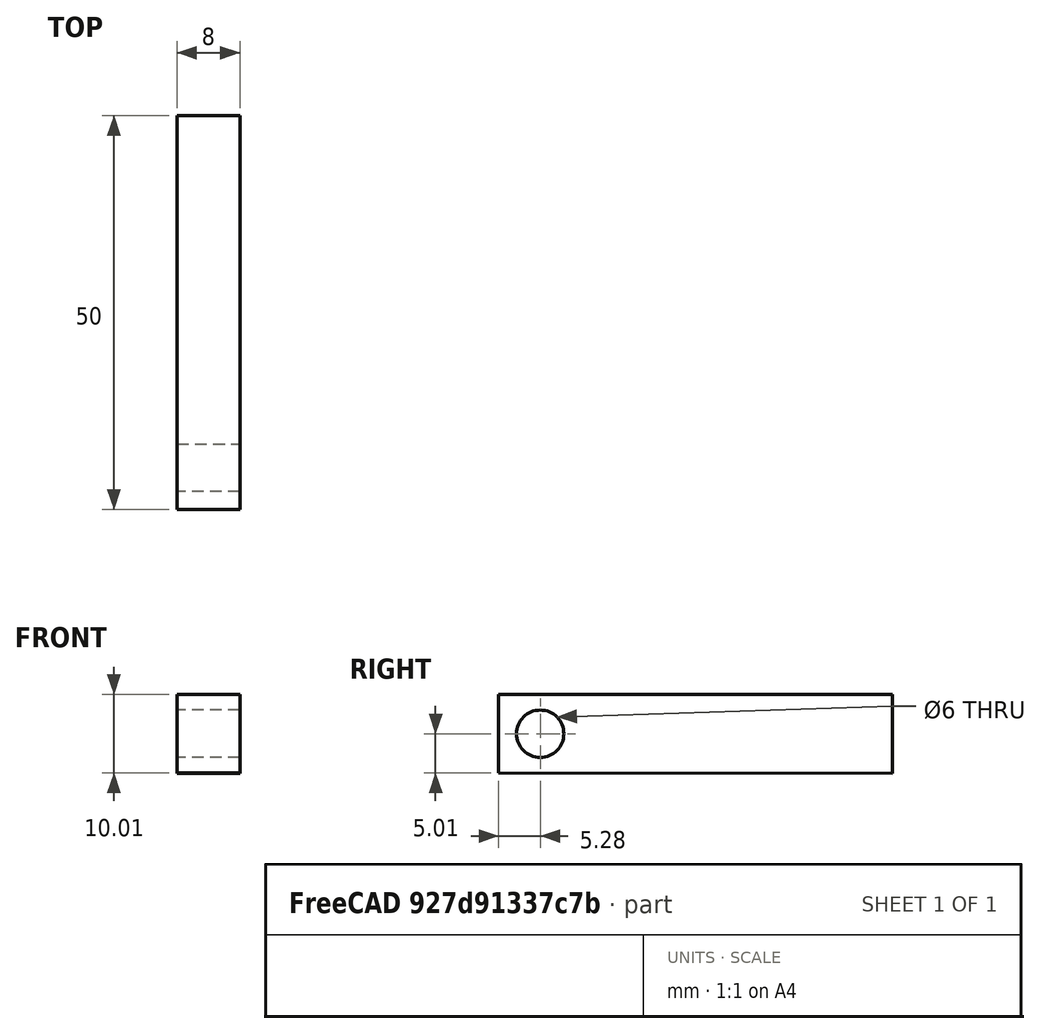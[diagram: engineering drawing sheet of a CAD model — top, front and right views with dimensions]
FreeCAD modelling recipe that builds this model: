
FCSTD DOCUMENT  (FreeCAD 0.21R33668 +26 (Git))
Label: Assembly_001
License: All rights reserved
LicenseURL: http://en.wikipedia.org/wiki/All_rights_reserved
objects: PartDesign::CoordinateSystem×6, App::DocumentObjectGroup×3, App::Part×3, Sketcher::SketchObject×2, App::Link×2, App::FeaturePython×1, PartDesign::Pad×1, PartDesign::Body×1
note: 11 computed .brp shape members not serialized (recipe doc carries the construction recipe); baked Part::Feature solids carry a one-line shape summary decoded from their .brp

FEATURE [PartDesign::CoordinateSystem] LCS_Origin
  AttacherType = Attacher::AttachEngine3D
  MapMode = 2
  Support = -> [X_Axis]
FEATURE [App::DocumentObjectGroup] Constraints
FEATURE [App::FeaturePython] Variables  # WARN: FeaturePython — macro-defined, semantics opaque (R4)
  Type = App::PropertyContainer
  rotation_bielle = 324
FEATURE [App::DocumentObjectGroup] Configurations
FEATURE [PartDesign::CoordinateSystem] LCS_0
  AttacherType = Attacher::AttachEngine3D
  MapMode = 2
  Support = -> [X_Axis001]
FEATURE [Sketcher::SketchObject] Sketch
  FullyConstrained = false
  MapMode = 5
  Placement = pos=(0,0,0) rot=(0.57735,0.57735,0.57735;2.0944rad)
  Support = -> [YZ_Plane001]
  sketch-geometry (5):
    g0: LineSegment StartX=-5.27726 StartY=5.00146 StartZ=0 EndX=44.7227 EndY=4.98767 EndZ=0
    g1: LineSegment StartX=44.7227 StartY=4.98767 StartZ=0 EndX=44.72 EndY=-5.01233 EndZ=0
    g2: LineSegment StartX=44.72 StartY=-5.01233 StartZ=0 EndX=-5.28002 EndY=-4.99854 EndZ=0
    g3: LineSegment StartX=-5.28002 StartY=-4.99854 StartZ=0 EndX=-5.27726 EndY=5.00146 EndZ=0
    g4: Circle CenterX=0 CenterY=0 CenterZ=0 NormalX=0 NormalY=0 NormalZ=1 AngleXU=0 Radius=3
  constraints (13):
    c: Coincident(g0,g1)
    c: Coincident(g1,g2)
    c: Coincident(g2,g3)
    c: Coincident(g3,g0)
    c: Distance(g0,g2) = 10
    c: Distance(g0,g0) = 50
    c: Parallel(g0,g2)
    c: Parallel(g3,g1)
    c: Perpendicular(g0,g1)
    c: Coincident(g4,g-1)
    c: Radius(g4) = 3
    c: Distance(g4,g0) = 45
    c: Distance(g4,g1) = 45
FEATURE [PartDesign::Pad] Pad
  Direction = (1,-2e-16,3e-16)
  Length = 8
  Length2 = 10
  Placement = pos=(0,0,0) rot=(0.57735,0.57735,0.57735;2.0944rad)
  Profile = -> Sketch
  ReferenceAxis = -> Sketch [N_Axis]
  Type = 0
FEATURE [PartDesign::Body] Body
  Group = -> [LCS_0,Sketch,Pad]
  Origin = -> Origin001
  Placement = pos=(-52,0,0) rot=(0,0,1;0rad)
  Tip = -> Pad
FEATURE [App::DocumentObjectGroup] Parts
  Group = -> [Body]
FEATURE [Sketcher::SketchObject] Sketch_1
  FullyConstrained = true
  MapMode = 5
  Placement = pos=(0,0,0) rot=(0.57735,0.57735,0.57735;2.0944rad)
  Support = -> [YZ_Plane]
  expr: Constraints[4] = Variables.rotation_bielle
  expr: Constraints[5] = Variables.rotation_bielle - 90
  sketch-geometry (2):
    g0: LineSegment StartX=0 StartY=0 StartZ=0 EndX=28.3156 EndY=-20.5725 EndZ=0
    g1: LineSegment StartX=0 StartY=0 StartZ=0 EndX=-29.3893 EndY=40.4508 EndZ=0
  constraints (6):
    c: Coincident(g0,g-1)
    c: Distance(g0,g0) = 35
    c: Coincident(g1,g0)
    c: Distance(g0,g1) = 50
    c: Angle(g-1,g0) = 5.65487
    c: Angle(g1,g-1) = 4.08407
FEATURE [PartDesign::CoordinateSystem] LCS_1  label="LCS_bielle_1"
  AttacherType = Attacher::AttachEngine3D
  MapMode = 7
  Placement = pos=(0,0,0) rot=(1,0,0;0.628319rad)
  Support = -> [Sketch_1]
FEATURE [App::Link] Body001
  AttachedBy = #LCS_0
  AttachedTo = Parent Assembly#LCS_1
  AttachmentOffset = pos=(0,0,0) rot=(1,0,0;4.71239rad)
  ColoredElements = -> Body001
  LinkPlacement = pos=(0,0,0) rot=(1,0,0;5.34071rad)
  LinkedObject = -> Body
  Placement = pos=(0,0,0) rot=(1,0,0;5.34071rad)
  SolverId = Asm4EE
  expr: Placement = LCS_1.Placement * AttachmentOffset * LCS_0.Placement ^ -1
FEATURE [PartDesign::CoordinateSystem] LCS_bielle_2
  AttacherType = Attacher::AttachEngine3D
  MapMode = 7
  Placement = pos=(0,0,0) rot=(1,0,0;0.942478rad)
  Support = -> [Sketch_1]
FEATURE [App::Link] Body002
  AttachedBy = #LCS_0
  AttachedTo = Parent Assembly#LCS_bielle_2
  AttachmentOffset = pos=(0,0,0) rot=(1,0,0;4.71239rad)
  LinkPlacement = pos=(0,0,0) rot=(1,0,0;5.65487rad)
  LinkedObject = -> Body
  Placement = pos=(0,0,0) rot=(1,0,0;5.65487rad)
  SolverId = Asm4EE
  expr: Placement = LCS_bielle_2.Placement * AttachmentOffset * LCS_0.Placement ^ -1
FEATURE [PartDesign::CoordinateSystem] LCS_002
  AttacherType = Attacher::AttachEngine3D
  MapMode = 2
  Support = -> [X_Axis002]
FEATURE [App::Part] Part001
  Group = -> [LCS_002,Body001]
  Origin = -> Origin002
FEATURE [PartDesign::CoordinateSystem] LCS_003
  AttacherType = Attacher::AttachEngine3D
  MapMode = 2
  Support = -> [X_Axis003]
FEATURE [App::Part] Part002
  Group = -> [LCS_003,Body002]
  Origin = -> Origin003
  Placement = pos=(8,0,0) rot=(0,0,1;0rad)
FEATURE [App::Part] Assembly
  AssemblyType = Part::Link
  Group = -> [LCS_Origin,Constraints,Variables,Configurations,Sketch_1,LCS_1,LCS_bielle_2,Part001,Part002]
  Origin = -> Origin
  Type = Assembly
